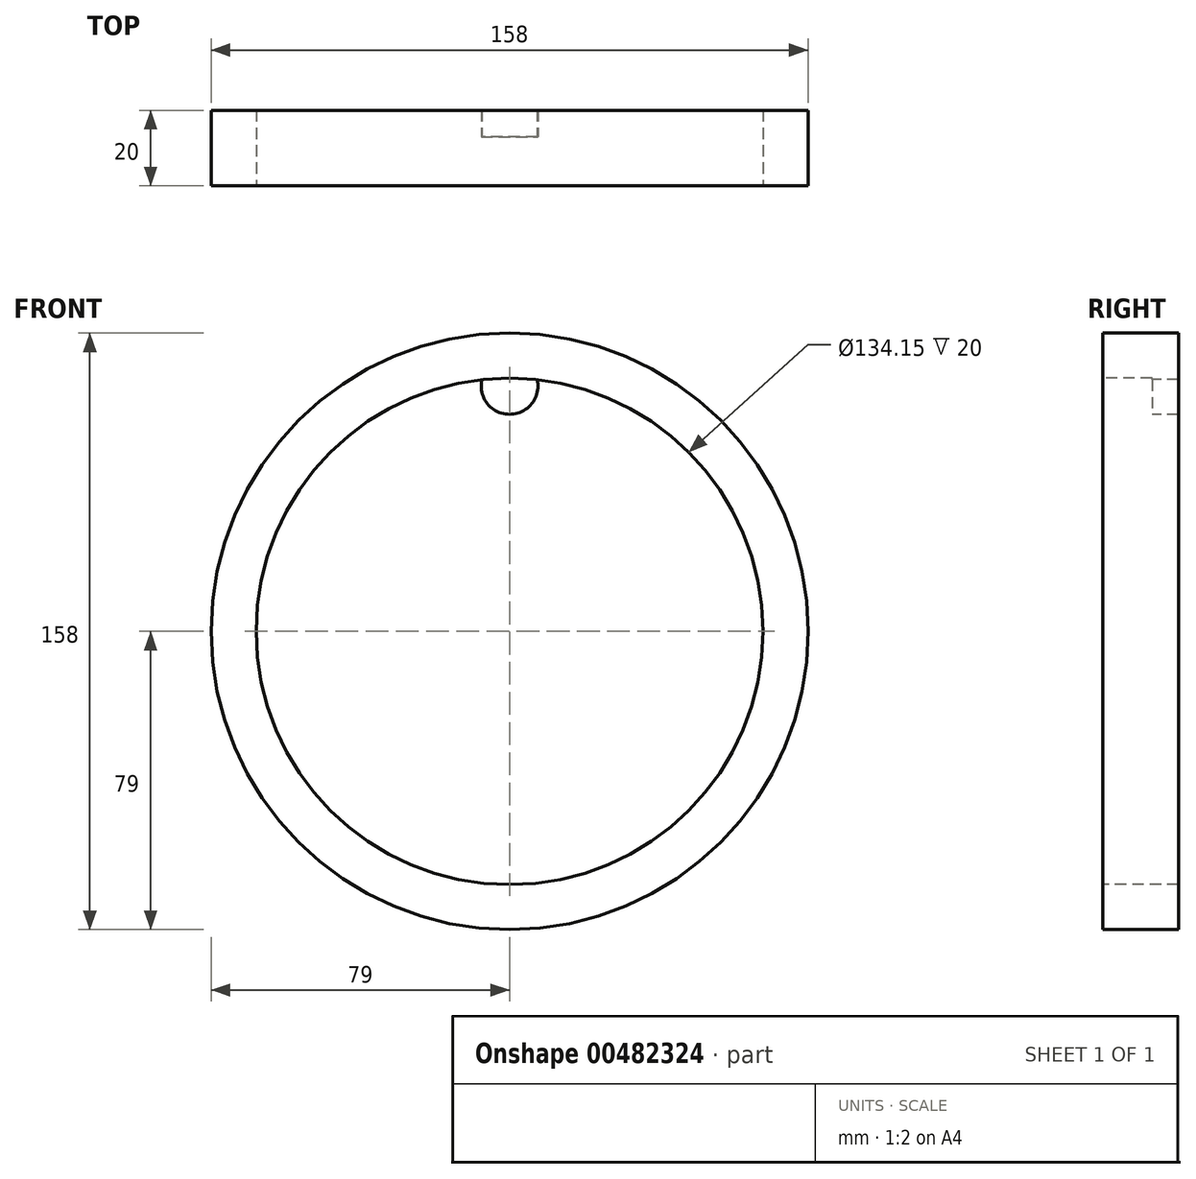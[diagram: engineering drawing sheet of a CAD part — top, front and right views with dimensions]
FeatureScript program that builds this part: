
annotation { "Feature Type Name" : "Feature", "Feature Type Description" : "" }
export const myFeature = defineFeature(function(context is Context, id is Id, definition is map)
    precondition{}
    {
        {
            var Q0;
            Q0=qCreatedBy(makeId("Front.planeOp"),FACE);
            var sketch = newSketch(context, id + "F0", { "sketchPlane" : qUnion([Q0])});
            skCircle(sketch, "E0", {"center": v(0, 0) * mm, "radius": 33 * mm});
            skCircle(sketch, "E1", {"center": v(0, 0) * mm, "radius": 79 * mm});
            skSolve(sketch);
        }
        {
            var Q0;
            Q0=makeQuery(id+"F0.imprint","IMPRINT",FACE,{"disambiguationData":[TD([[makeQuery(id+"F0.imprint","IMPRINT",EDGE,{"derivedFrom":sQuery(id+"F0.wireOp",EDGE,"E0")}),-1.0]])]});
            extrude(context, id + "F1", {"entities" : qUnion([Q0]), "depth" : 20 * mm});
        }
        {
            var Q0;
            Q0=makeQuery(id+"F1.opExtrude","CAP_FACE",FACE,{"disambiguationData":[OSD([sQuery(id+"F0.wireOp",EDGE,"E0"),sQuery(id+"F0.wireOp",EDGE,"E1")])],"isStart":false});
            var sketch = newSketch(context, id + "F2", { "sketchPlane" : qUnion([Q0])});
            skCircle(sketch, "E2", {"center": v(0, 0) * mm, "radius": 67.08 * mm});
            skSolve(sketch);
        }
        {
            var Q0;
            Q0 = qSketchRegion(id + "F2", true);
            extrude(context, id + "F3", {"entities" : qUnion([Q0]), "operationType" : NewBodyOperationType.REMOVE, "oppositeDirection" : true, "depth" : 13 * mm});
        }
        {
            var Q0;
            Q0=makeQuery(id+"F3.boolean.opBoolean","INTERSECT",EDGE,{"derivedFrom":[makeQuery(id+"F1.opExtrude","SWEPT_FACE",FACE,{"disambiguationData":[OSD([sQuery(id+"F0.wireOp",EDGE,"E0")])]}),makeQuery(id+"F3.opExtrude","CAP_FACE",FACE,{"disambiguationData":[OSD([sQuery(id+"F2.wireOp",EDGE,"E2")])],"isStart":false})]});
            chamfer(context, id + "F4", {"entities" : qUnion([Q0]), "width" : 5 * mm});
        }
        {
            var Q0;
            Q0=makeQuery(id+"F1.opExtrude","CAP_FACE",FACE,{"disambiguationData":[OSD([sQuery(id+"F0.wireOp",EDGE,"E0"),sQuery(id+"F0.wireOp",EDGE,"E1")])],"isStart":false});
            var sketch = newSketch(context, id + "F5", { "sketchPlane" : qUnion([Q0])});
            skCircle(sketch, "E3", {"center": v(0, 0) * mm, "radius": 65 * mm});
            skCircle(sketch, "E4", {"center": v(0, 65) * mm, "radius": 7.5 * mm});
            skSolve(sketch);
        }
        {
            var Q0;
            {var subQ0=sQuery(id+"F5.wireOp",EDGE,"E4");var subQ1=makeQuery(id+"F3.boolean.opBoolean","COPY",EDGE,{"derivedFrom":makeQuery(id+"F3.opExtrude","CAP_EDGE",EDGE,{"disambiguationData":[OSD([sQuery(id+"F2.wireOp",EDGE,"E2")])],"isStart":true})});var subQ2=makeQuery(id+"F5.imprint","INTERSECT",VERTEX,{"disambiguationData":[OD(0.0)],"derivedFrom":[subQ1,subQ0]});Q0=makeQuery(id+"F5.imprint","IMPRINT",FACE,{"disambiguationData":[TD([[makeQuery(id+"F5.imprint","IMPRINT",EDGE,{"disambiguationData":[TD([[subQ2,1.0]])],"derivedFrom":subQ0}),1.0]])]});}
            var Q1;
            {var subQ0=sQuery(id+"F5.wireOp",EDGE,"E4");var subQ1=sQuery(id+"F5.wireOp",EDGE,"E3");var subQ2=makeQuery(id+"F5.imprint","INTERSECT",VERTEX,{"disambiguationData":[OD(0.0)],"derivedFrom":[subQ1,subQ0]});Q1=makeQuery(id+"F5.imprint","IMPRINT",FACE,{"disambiguationData":[TD([[makeQuery(id+"F5.imprint","IMPRINT",EDGE,{"disambiguationData":[TD([[subQ2,1.0]])],"derivedFrom":subQ1}),1.0]])]});}
            var Q2;
            {var subQ0=sQuery(id+"F5.wireOp",EDGE,"E4");var subQ1=sQuery(id+"F5.wireOp",EDGE,"E3");var subQ2=makeQuery(id+"F5.imprint","INTERSECT",VERTEX,{"disambiguationData":[OD(0.0)],"derivedFrom":[subQ1,subQ0]});Q2=makeQuery(id+"F5.imprint","IMPRINT",FACE,{"disambiguationData":[TD([[makeQuery(id+"F5.imprint","IMPRINT",EDGE,{"disambiguationData":[TD([[subQ2,1.0]])],"derivedFrom":subQ1}),-1.0]])]});}
            extrude(context, id + "F6", {"entities" : qUnion([Q0, Q1, Q2]), "operationType" : NewBodyOperationType.REMOVE, "endBound" : BoundingType.THROUGH_ALL, "oppositeDirection" : true, "depth" : 25 * mm});
        }
    });
